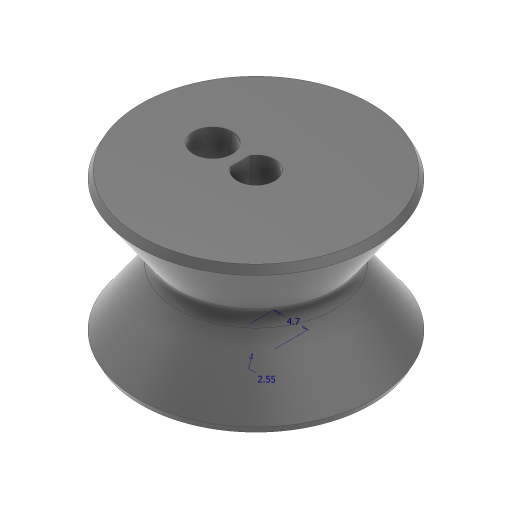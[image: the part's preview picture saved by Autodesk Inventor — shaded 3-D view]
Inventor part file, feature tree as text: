
AUTODESK INVENTOR PART (.ipt)
format: ipt  version: 2023 (Build 270158000, 158)  size: 291,328 bytes
history: native  units: mm
features: sketch x3, chamfer x3, plane x2, revolve x1, extrude x1, sweep x1, fillet x1, hole x1
ambient origin geometry x8: Origin, YZ Plane, XZ Plane, XY Plane, X Axis, Y Axis, Z Axis, Center Point
bodies: Solid1 (feature_tree)
feature tree (13):
  sketch  "Sketch1"  dims[d1=4.7mm d4=20.0mm]
  revolve  "Revolution1"  [1 undecoded]
  extrude  "Extrusion1"  Depth=14.0mm
  chamfer  "Chamfer1"  [1 undecoded]
  plane  "Work Plane3"
  sweep  "Sweep1"
  plane  "Work Plane4"
  fillet  "Fillet1"  Radius=3.490659mm
  chamfer  "Chamfer2"  [1 undecoded]
  hole  "Hole4"  [1 undecoded]
  chamfer  "Chamfer3"  [1 undecoded]
  sketch  "Sketch8"  dims[d5=14.0mm d6=14.0mm]
  sketch  "Sketch9"  dims[d7=90.0deg d8=0.0mm d9=0.0mm d10=1.2mm d11=2.0mm d12=45.0deg d15=30.0deg d20=3.490659mm d71=-12.0mm d72=5.3mm d73=0.0mm d74=0.0mm d92=2.55mm d93=10.0mm d95=2.0mm d98=1.0mm d99=2.0mm d100=45.0deg d102=9.599311mm d103=10.0mm d105=6.5mm d106=6.0mm d107=6.0mm d108=2.0mm d109=90.0deg d110=5.3mm d111=0.0mm d112=0.2mm d113=2.0mm d114=45.0deg]
note: 5 required parameter values undecoded (feature->parameter linkage not recoverable at this tier; creation-order binding heuristic only, values carry confidence <= 0.55)